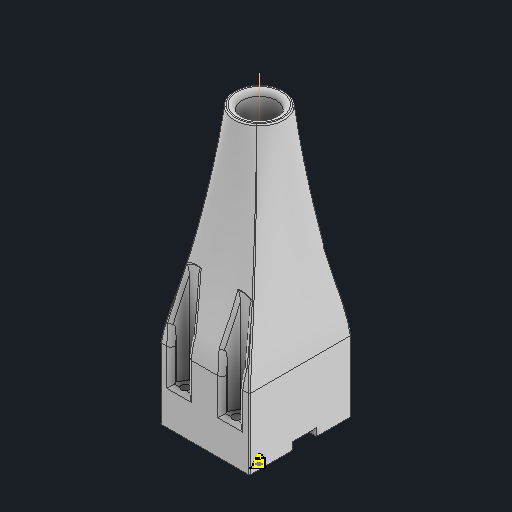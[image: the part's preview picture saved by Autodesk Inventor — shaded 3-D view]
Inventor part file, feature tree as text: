
AUTODESK INVENTOR PART (.ipt)
format: ipt  version: 2024.1 (Build 281209000, 209)  size: 6,007,296 bytes
history: native  units: mm
features: projected_geometry x26, sketch x25, extrude x15, fillet x14, loft x6, plane x4, thicken_offset x2, boolean_combine x1, other x1
ambient origin geometry x8: Origin, YZ Plane, XZ Plane, XY Plane, X Axis, Y Axis, Z Axis, Center Point
bodies: Solid1 (feature_tree), Solid3 (feature_tree), Solid4 (feature_tree)
feature tree (94):
  extrude  "Extrusion1"  Depth=3.0mm
  extrude  "Extrusion2"  TaperAngle=0.0deg  [1 undecoded]
  extrude  "Extrusion3"  Depth=10.0mm TaperAngle=0.0deg
  extrude  "Extrusion4"  Depth=0.5mm
  extrude  "Extrusion5"  Depth=0.5mm
  sketch  "Sketch6"  dims[d14=0.5mm d15=0.5mm]
  plane  "Work Plane1"
  loft  "Loft1"
  loft  "Loft2"
  extrude  "Extrusion6"  Depth=0.5mm
  extrude  "Extrusion8"  Depth=0.5mm
  extrude  "Extrusion9"  Depth=0.5mm
  extrude  "Extrusion10"  Depth=0.5mm
  extrude  "Extrusion11"  Depth=0.5mm
  extrude  "Extrusion12"  Depth=0.5mm
  plane  "Work Plane2"
  sketch  "Sketch19"  dims[d34=0.5mm d35=0.5mm]
  sketch  "Sketch20"  dims[d36=0.5mm d37=0.5mm]
  loft  "Loft3"
  loft  "Loft4"
  sketch  "Sketch22"  dims[d38=10.0mm d39=0.0mm d40=12.0mm]
  sketch  "Sketch23"  dims[d41=105.0mm d42=13.6mm d43=3.0mm d44=3.0mm d45=0.0mm d46=90.0deg d47=0.0mm d48=90.0deg d49=13.6mm d50=0.0mm d51=90.0deg d52=0.0mm d53=90.0deg d55=7.0mm d56=17.0mm d57=14.0mm d58=0.0mm d59=0.0mm d64=25.0mm d65=0.0mm]
  plane  "Work Plane3"
  plane  "Work Plane4"
  loft  "Loft5"
  loft  "Loft6"
  extrude  "Extrusion17"  Depth=10.0mm
  extrude  "Extrusion18"  Depth=3.0mm
  boolean_combine  "Combine1"
  fillet  "Fillet5"  Radius=3.0mm
  fillet  "Fillet6"  Radius=3.0mm
  fillet  "Fillet7"  [1 undecoded]
  fillet  "Fillet8"  [1 undecoded]
  fillet  "Fillet9"  Radius=13.6mm
  fillet  "Fillet10"  [1 undecoded]
  fillet  "Fillet11"  [1 undecoded]
  fillet  "Fillet13"  Radius=7.0mm
  fillet  "Fillet14"  Radius=17.0mm
  fillet  "Fillet16"  Radius=14.0mm
  thicken_offset  "Thicken1"
  fillet  "Fillet17"  [1 undecoded]
  thicken_offset  "Thicken2"
  fillet  "Fillet18"  Radius=25.0mm
  extrude  "Extrusion19"  Depth=3.0mm TaperAngle=0.0deg
  fillet  "Fillet19"  Radius=3.0mm
  extrude  "Extrusion20"  TaperAngle=0.0deg  [1 undecoded]
  fillet  "Fillet20"  Radius=10.0mm
  sketch  "Sketch1"  dims[d0=3.0mm d1=0.0mm d2=0.2mm]
  sketch  "Sketch2"  dims[d3=1.0mm d4=0.0mm d5=0.0mm]
  sketch  "Sketch3"  dims[d6=10.0mm d7=0.0mm d8=10.0mm d9=0.0mm]
  sketch  "Sketch4"  dims[d10=0.5mm d11=0.5mm]
  sketch  "Sketch5"  dims[d12=0.5mm d13=0.5mm]
  sketch  "Sketch7"  dims[d16=0.5mm d17=0.5mm]
  sketch  "Sketch8"  dims[d18=0.5mm d19=0.5mm]
  sketch  "Sketch9"  dims[d20=0.5mm d21=0.5mm]
  sketch  "Sketch11"  dims[d22=0.5mm d23=0.5mm]
  sketch  "Sketch13"  dims[d24=0.5mm d25=0.5mm]
  projected_geometry  "Projected Loop2"
  projected_geometry  "Projected Loop3"
  projected_geometry  "Projected Loop4"
  projected_geometry  "Projected Loop5"
  projected_geometry  "Projected Loop6"
  projected_geometry  "Projected Loop7"
  projected_geometry  "Projected Loop8"
  projected_geometry  "Projected Loop9"
  projected_geometry  "Projected Loop10"
  projected_geometry  "Projected Loop11"
  projected_geometry  "Projected Loop12"
  projected_geometry  "Projected Loop13"
  projected_geometry  "Projected Loop14"
  projected_geometry  "Projected Loop15"
  projected_geometry  "Projected Loop16"
  projected_geometry  "Projected Loop17"
  sketch  "Sketch14"  dims[d26=0.5mm d27=0.5mm]
  sketch  "Sketch15"  dims[d28=0.5mm d29=0.5mm]
  projected_geometry  "Projected Loop18"
  sketch  "Sketch16"  dims[d30=0.5mm d31=0.5mm]
  sketch  "Sketch17"  dims[d32=0.5mm d33=0.5mm]
  projected_geometry  "Projected Loop19"
  sketch  "Sketch24"  dims[d66=25.0mm d67=0.0mm d68=25.0mm d69=0.0mm d70=3.0mm]
  sketch  "Sketch25"  dims[d71=1.0mm d72=0.0mm d73=10.0mm d74=0.0mm]
  other  "Work Axis2"
  sketch  "Sketch26"  dims[d75=10.0mm d76=0.0mm]
  sketch  "Sketch27"  dims[d84=0.0mm d85=90.0deg]
  sketch  "Sketch28"  dims[d86=0.0mm d87=90.0deg]
  sketch  "Sketch29"  dims[d88=0.0mm d89=90.0deg d90=0.0mm d91=90.0deg d104=0.0mm d105=90.0deg d106=0.0mm d107=90.0deg d108=0.0mm d109=90.0deg d110=0.0mm d111=90.0deg d112=10.0mm d113=0.0mm d118=0.0mm d123=10.0mm d124=10.0mm d125=0.0mm d126=90.0deg d127=0.0mm d128=90.0deg d133=10.0mm d134=10.0mm d135=0.0mm d136=90.0deg d137=0.0mm d138=90.0deg d140=6.6mm d141=20.32mm d142=35.56mm d143=20.0mm d145=20.32mm d146=20.0mm d148=35.56mm d151=93.0mm d152=0.0mm d156=1.5mm d157=1.5mm d158=0.5mm d159=2.0mm d160=0.5mm d161=0.5mm d162=2.0mm d164=1.0mm d165=1.0mm d167=0.3mm d168=0.1mm d169=0.1mm d170=0.3mm d171=0.2mm d172=0.1mm d173=0.3mm d174=10.0mm d175=0.0mm d176=0.5mm d177=10.0mm d178=0.0mm d179=0.5mm d114=0.5mm d115=0.872665mm d155=0.0mm]
  projected_geometry  "Project Cut Edges1"
  projected_geometry  "Project Cut Edges2"
  projected_geometry  "Project Cut Edges3"
  projected_geometry  "Project Cut Edges5"
  projected_geometry  "Project Cut Edges6"
  projected_geometry  "Project Cut Edges7"
  projected_geometry  "Project Cut Edges8"
  projected_geometry  "Project Cut Edges9"
note: 7 required parameter values undecoded (feature->parameter linkage not recoverable at this tier; creation-order binding heuristic only, values carry confidence <= 0.55)
